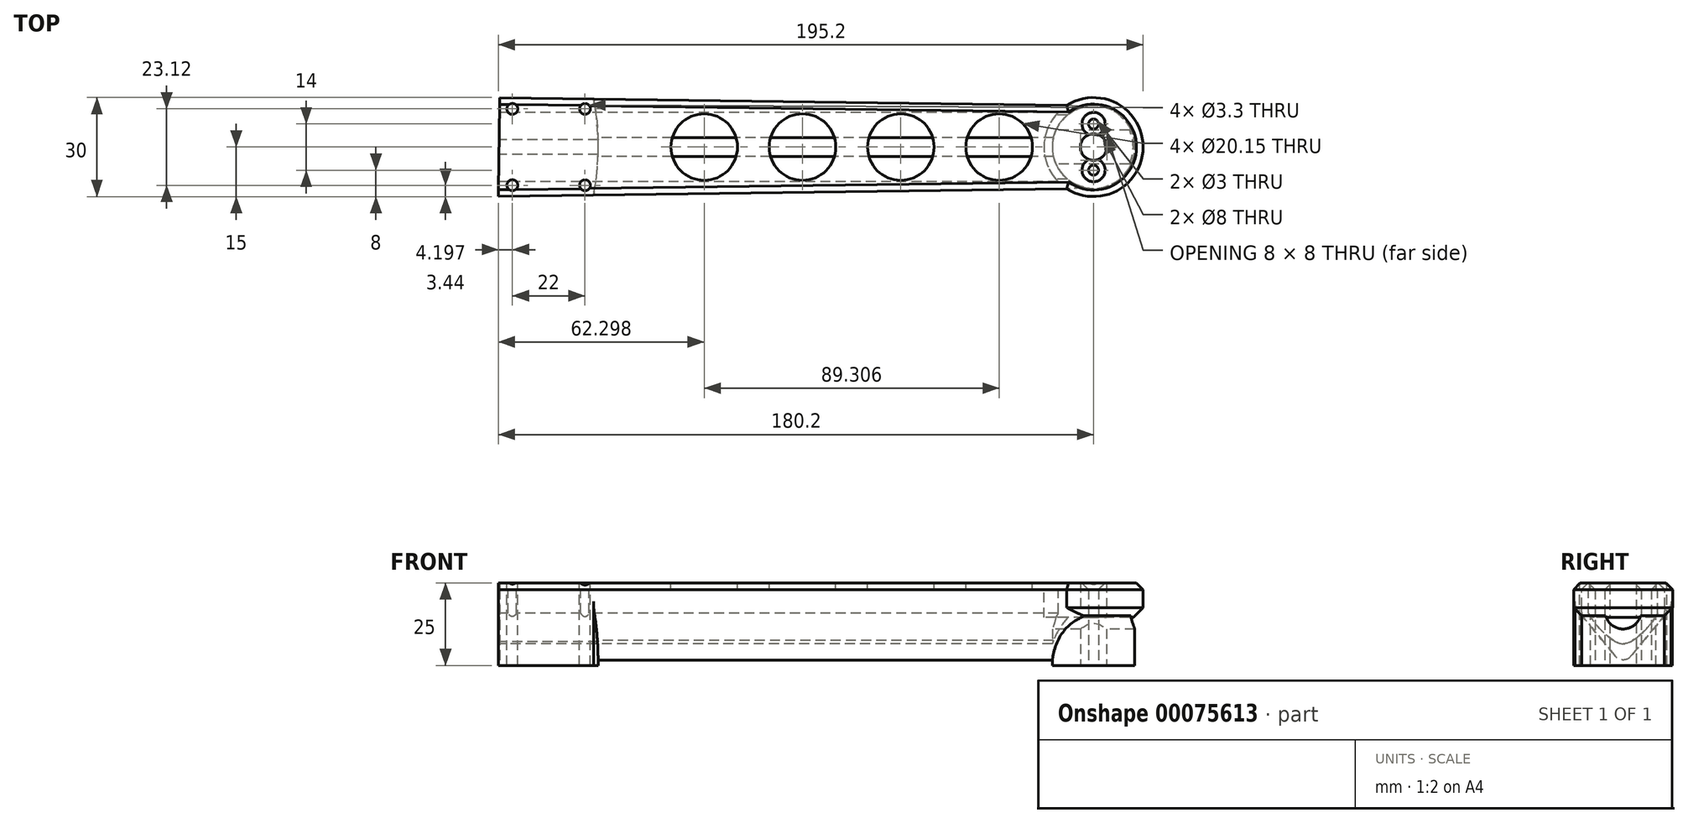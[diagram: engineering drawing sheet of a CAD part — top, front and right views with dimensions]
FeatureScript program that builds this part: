
annotation { "Feature Type Name" : "Feature", "Feature Type Description" : "" }
export const myFeature = defineFeature(function(context is Context, id is Id, definition is map)
    precondition{}
    {
        {
            var Q0;
            Q0=qCreatedBy(makeId("Top.planeOp"),FACE);
            var sketch = newSketch(context, id + "F0", { "sketchPlane" : qUnion([Q0])});
            skArc(sketch, "E0", {"start": v(73.58, -14.53) * mm, "mid": v(75, 0) * mm, "end": v(73.58, 14.53) * mm});
            skCircle(sketch, "E1", {"center": v(225, 0) * mm, "radius": 12.5 * mm});
            skLineSegment(sketch, "E2", {"start": v(224.65, 12.5) * mm, "end": v(45.2, 14.9) * mm});
            skLineSegment(sketch, "E3.MirrorCS", {"start": v(224.65, -12.5) * mm, "end": v(44.8, -14.91) * mm});
            skLineSegment(sketch, "E4", {"start": v(45.2, 14.9) * mm, "end": v(44.8, -14.91) * mm});
            skPoint(sketch, "E5.orphan", {"position": v(38.3, 15) * mm});
            skPoint(sketch, "E6.orphan", {"position": v(38.3, -15) * mm});
            skSolve(sketch);
        }
        {
            var Q0;
            {var subQ0=sQuery(id+"F0.wireOp",EDGE,"E0");Q0=makeQuery(id+"F0.imprint","IMPRINT",FACE,{"disambiguationData":[TD([[makeQuery(id+"F0.imprint","IMPRINT",EDGE,{"derivedFrom":subQ0}),-1.0]])]});}
            extrude(context, id + "F1", {"entities" : qUnion([Q0]), "depth" : 25 * mm});
        }
        {
            var Q0;
            Q0=qCreatedBy(makeId("Right.planeOp"),FACE);
            var sketch = newSketch(context, id + "F2", { "sketchPlane" : qUnion([Q0])});
            skLineSegment(sketch, "E7", {"start": v(-36.38, 18) * mm, "end": v(32.2, 18) * mm, "construction": true});
            skLineSegment(sketch, "E8", {"start": v(-14.91, 18) * mm, "end": v(-2.26, 2.72) * mm});
            skLineSegment(sketch, "E9.MirrorCS", {"start": v(14.91, 18) * mm, "end": v(2.26, 2.72) * mm});
            skPoint(sketch, "E10.visualSharp", {"position": v(0, 0) * mm});
            skArc(sketch, "E10.filletArc", {"start": v(-2.26, 2.72) * mm, "mid": v(0, 1.66) * mm, "end": v(2.26, 2.72) * mm});
            skLineSegment(sketch, "E11", {"start": v(14.91, 18) * mm, "end": v(14.91, -2.4) * mm});
            skLineSegment(sketch, "E12", {"start": v(14.91, -2.4) * mm, "end": v(-14.91, -2.4) * mm});
            skLineSegment(sketch, "E13", {"start": v(-14.91, -2.4) * mm, "end": v(-14.91, 18) * mm});
            skSolve(sketch);
        }
        {
            var Q0;
            Q0 = qSketchRegion(id + "F2", true);
            extrude(context, id + "F3", {"entities" : qUnion([Q0]), "operationType" : NewBodyOperationType.REMOVE, "endBound" : BoundingType.THROUGH_ALL, "depth" : 25 * mm});
        }
        {
            var Q0;
            Q0=qCreatedBy(makeId("Right.planeOp"),FACE);
            var sketch = newSketch(context, id + "F4", { "sketchPlane" : qUnion([Q0])});
            skLineSegment(sketch, "E14", {"start": v(10.5, 23) * mm, "end": v(-10.5, 23) * mm});
            skPoint(sketch, "E15.orphan", {"position": v(12.88, 17.57) * mm});
            skPoint(sketch, "E16.orphan", {"position": v(-12.88, 17.57) * mm});
            skArc(sketch, "E17", {"start": v(-2.82, 7.54) * mm, "mid": v(0, 6.6) * mm, "end": v(2.82, 7.54) * mm});
            skLineSegment(sketch, "E18", {"start": v(-10.5, 23) * mm, "end": v(-10.5, 15.85) * mm});
            skLineSegment(sketch, "E19.MirrorCS", {"start": v(10.5, 23) * mm, "end": v(10.5, 15.85) * mm});
            skPoint(sketch, "E20.orphan", {"position": v(-12.88, 23) * mm});
            skPoint(sketch, "E21.orphan", {"position": v(-10.5, 23.41) * mm});
            skPoint(sketch, "E22.orphan", {"position": v(-10.5, 15.28) * mm});
            skPoint(sketch, "E23.end.orphan", {"position": v(12.88, 23) * mm});
            skPoint(sketch, "E24.orphan", {"position": v(10.5, 15.28) * mm});
            skPoint(sketch, "E25.orphan", {"position": v(10.5, 23.41) * mm});
            skArc(sketch, "E26", {"start": v(2.2, 7.15) * mm, "mid": v(6.91, 10.96) * mm, "end": v(10.5, 15.85) * mm});
            skArc(sketch, "E27.MirrorCS", {"start": v(-2.2, 7.15) * mm, "mid": v(-6.91, 10.96) * mm, "end": v(-10.5, 15.85) * mm});
            skPoint(sketch, "E28.center.orphan", {"position": v(0, 25.65) * mm});
            skSolve(sketch);
        }
        {
            var Q0;
            Q0 = qSketchRegion(id + "F4", true);
            extrude(context, id + "F5", {"entities" : qUnion([Q0]), "operationType" : NewBodyOperationType.REMOVE, "endBound" : BoundingType.THROUGH_ALL, "depth" : 25 * mm, "hasSecondDirection" : true, "secondDirectionBound" : SecondDirectionBoundingType.THROUGH_ALL, "secondDirectionOppositeDirection" : true, "secondDirectionDepth" : 25 * mm});
        }
        {
            var Q0;
            Q0=makeQuery(id+"F1.opExtrude","CAP_FACE",FACE,{"disambiguationData":[OSD([sQuery(id+"F0.wireOp",EDGE,"E0"),sQuery(id+"F0.wireOp",EDGE,"E1"),sQuery(id+"F0.wireOp",EDGE,"E2"),sQuery(id+"F0.wireOp",EDGE,"E3.MirrorCS")])],"isStart":false});
            var sketch = newSketch(context, id + "F6", { "sketchPlane" : qUnion([Q0])});
            skCircle(sketch, "E29", {"center": v(107.1, 0) * mm, "radius": 10.07 * mm});
            skCircle(sketch, "E30.1.0.0", {"center": v(136.87, 0) * mm, "radius": 10.07 * mm});
            skCircle(sketch, "E30.2.0.0", {"center": v(166.64, 0) * mm, "radius": 10.07 * mm});
            skCircle(sketch, "E30.3.0.0", {"center": v(196.4, 0) * mm, "radius": 10.07 * mm});
            skLineSegment(sketch, "E30.direction1", {"start": v(107.1, 0) * mm, "end": v(136.87, 0) * mm, "construction": true});
            skSolve(sketch);
        }
        {
            var Q0;
            Q0=makeQuery(id+"F6.imprint","IMPRINT",FACE,{"disambiguationData":[TD([[makeQuery(id+"F6.imprint","IMPRINT",EDGE,{"derivedFrom":sQuery(id+"F6.wireOp",EDGE,"E30.3.0.0")}),1.0]])]});
            var Q1;
            Q1=makeQuery(id+"F6.imprint","IMPRINT",FACE,{"disambiguationData":[TD([[makeQuery(id+"F6.imprint","IMPRINT",EDGE,{"derivedFrom":sQuery(id+"F6.wireOp",EDGE,"E30.2.0.0")}),1.0]])]});
            var Q2;
            Q2=makeQuery(id+"F6.imprint","IMPRINT",FACE,{"disambiguationData":[TD([[makeQuery(id+"F6.imprint","IMPRINT",EDGE,{"derivedFrom":sQuery(id+"F6.wireOp",EDGE,"E30.1.0.0")}),1.0]])]});
            var Q3;
            Q3=makeQuery(id+"F6.imprint","IMPRINT",FACE,{"disambiguationData":[TD([[makeQuery(id+"F6.imprint","IMPRINT",EDGE,{"derivedFrom":sQuery(id+"F6.wireOp",EDGE,"E29")}),1.0]])]});
            var Q4;
            Q4=makeQuery(id+"F5.boolean.opBoolean","COPY",FACE,{"derivedFrom":makeQuery(id+"F5.opExtrude","SWEPT_FACE",FACE,{"disambiguationData":[OSD([sQuery(id+"F4.wireOp",EDGE,"E17")])]})});
            extrude(context, id + "F7", {"entities" : qUnion([Q0, Q1, Q2, Q3]), "operationType" : NewBodyOperationType.REMOVE, "oppositeDirection" : true, "endBoundEntityFace" : qUnion([Q4]), "depth" : 7.95 * mm});
        }
        {
            var Q0;
            {var subQ0=sQuery(id+"F0.wireOp",EDGE,"E1");var subQ1=makeQuery(id+"F0.imprint","INTERSECT",VERTEX,{"derivedFrom":[subQ0,sQuery(id+"F0.wireOp",EDGE,"E2")]});Q0=makeQuery(id+"F0.imprint","IMPRINT",FACE,{"disambiguationData":[TD([[makeQuery(id+"F0.imprint","IMPRINT",EDGE,{"disambiguationData":[TD([[subQ1,-1.0]])],"derivedFrom":subQ0}),1.0]])]});}
            extrude(context, id + "F8", {"entities" : qUnion([Q0]), "operationType" : NewBodyOperationType.REMOVE, "depth" : 15.03 * mm});
        }
        {
            var Q0;
            {var subQ0=sQuery(id+"F0.wireOp",EDGE,"E0");Q0=makeQuery(id+"F0.imprint","IMPRINT",FACE,{"disambiguationData":[TD([[makeQuery(id+"F0.imprint","IMPRINT",EDGE,{"derivedFrom":subQ0}),1.0]])]});}
            extrude(context, id + "F9", {"entities" : qUnion([Q0]), "operationType" : NewBodyOperationType.ADD, "depth" : 25 * mm});
        }
        {
            var Q0;
            {var subQ0=sQuery(id+"F0.wireOp",EDGE,"E3.MirrorCS");var subQ1=sQuery(id+"F0.wireOp",EDGE,"E2");var subQ2=sQuery(id+"F0.wireOp",EDGE,"E0");var subQ3=sQuery(id+"F0.wireOp",EDGE,"E1");Q0=makeQuery(id+"F9.boolean.opBoolean","MERGE",FACE,{"derivedFrom":[makeQuery(id+"FpcsPqxv3NGoszD_1.boolean.opBoolean","MERGE",FACE,{"derivedFrom":[makeQuery(id+"F1.opExtrude","CAP_FACE",FACE,{"disambiguationData":[OSD([subQ2,subQ3,subQ1,subQ0])],"isStart":false}),makeQuery(id+"FpcsPqxv3NGoszD_1.opExtrude","CAP_FACE",FACE,{"disambiguationData":[OSD([subQ3])],"isStart":false})]}),makeQuery(id+"F9.opExtrude","CAP_FACE",FACE,{"disambiguationData":[OSD([subQ2,subQ1,subQ0,sQuery(id+"F0.wireOp",EDGE,"E4")])],"isStart":false})]});}
            var sketch = newSketch(context, id + "F10", { "sketchPlane" : qUnion([Q0])});
            skCircle(sketch, "E31", {"center": v(49, 11.56) * mm, "radius": 1.65 * mm});
            skCircle(sketch, "E32", {"center": v(71, 11.56) * mm, "radius": 1.65 * mm});
            skCircle(sketch, "E33.MirrorC", {"center": v(49, -11.56) * mm, "radius": 1.65 * mm});
            skCircle(sketch, "E34.MirrorC", {"center": v(71, -11.56) * mm, "radius": 1.65 * mm});
            skSolve(sketch);
        }
        {
            var Q0;
            Q0 = qSketchRegion(id + "F10", true);
            extrude(context, id + "F11", {"entities" : qUnion([Q0]), "operationType" : NewBodyOperationType.REMOVE, "oppositeDirection" : true, "depth" : 25 * mm});
        }
        {
            var Q0;
            {var subQ0=sQuery(id+"F0.wireOp",EDGE,"E3.MirrorCS");var subQ1=sQuery(id+"F0.wireOp",EDGE,"E2");var subQ2=sQuery(id+"F0.wireOp",EDGE,"E0");var subQ3=sQuery(id+"F0.wireOp",EDGE,"E1");Q0=makeQuery(id+"F9.boolean.opBoolean","MERGE",FACE,{"derivedFrom":[makeQuery(id+"FpcsPqxv3NGoszD_1.boolean.opBoolean","MERGE",FACE,{"derivedFrom":[makeQuery(id+"F1.opExtrude","CAP_FACE",FACE,{"disambiguationData":[OSD([subQ2,subQ3,subQ1,subQ0])],"isStart":false}),makeQuery(id+"FpcsPqxv3NGoszD_1.opExtrude","CAP_FACE",FACE,{"disambiguationData":[OSD([subQ3])],"isStart":false})]}),makeQuery(id+"F9.opExtrude","CAP_FACE",FACE,{"disambiguationData":[OSD([subQ2,subQ1,subQ0,sQuery(id+"F0.wireOp",EDGE,"E4")])],"isStart":false})]});}
            var sketch = newSketch(context, id + "F12", { "sketchPlane" : qUnion([Q0])});
            skCircle(sketch, "E35", {"center": v(225, 0) * mm, "radius": 3 * mm});
            skCircle(sketch, "E36", {"center": v(225, 7) * mm, "radius": 1.5 * mm});
            skCircle(sketch, "E37", {"center": v(225, -7) * mm, "radius": 1.5 * mm});
            skSolve(sketch);
        }
        {
            var Q0;
            Q0 = qSketchRegion(id + "F12", true);
            extrude(context, id + "F13", {"entities" : qUnion([Q0]), "operationType" : NewBodyOperationType.REMOVE, "oppositeDirection" : true, "depth" : 25 * mm});
        }
        {
            var Q0;
            Q0=makeQuery(id+"F4.imprint","IMPRINT",FACE,{"disambiguationData":[TD([[makeQuery(id+"F4.imprint","IMPRINT",EDGE,{"derivedFrom":sQuery(id+"F4.wireOp",EDGE,"E14")}),1.0]])]});
            extrude(context, id + "F14", {"entities" : qUnion([Q0]), "operationType" : NewBodyOperationType.REMOVE, "depth" : 84.6 * mm});
        }
        {
            var Q0;
            {var subQ0=sQuery(id+"F0.wireOp",EDGE,"E1");var subQ1=makeQuery(id+"F0.imprint","INTERSECT",VERTEX,{"derivedFrom":[subQ0,sQuery(id+"F0.wireOp",EDGE,"E2")]});Q0=makeQuery(id+"F0.imprint","IMPRINT",FACE,{"disambiguationData":[TD([[makeQuery(id+"F0.imprint","IMPRINT",EDGE,{"disambiguationData":[TD([[subQ1,-1.0]])],"derivedFrom":subQ0}),1.0]])]});}
            extrude(context, id + "F15", {"entities" : qUnion([Q0]), "operationType" : NewBodyOperationType.ADD, "depth" : 25 * mm});
        }
        {
            var Q0;
            Q0=qCreatedBy(makeId("Right.planeOp"),FACE);
            var sketch = newSketch(context, id + "F16", { "sketchPlane" : qUnion([Q0])});
            skCircle(sketch, "E38", {"center": v(0, 16.54) * mm, "radius": 5.49 * mm});
            skSolve(sketch);
        }
        {
            var Q0;
            Q0 = qSketchRegion(id + "F16", true);
            extrude(context, id + "F17", {"entities" : qUnion([Q0]), "operationType" : NewBodyOperationType.REMOVE, "endBound" : BoundingType.THROUGH_ALL, "depth" : 25 * mm});
        }
        {
            var Q0;
            {var subQ0=sQuery(id+"F0.wireOp",EDGE,"E1");var subQ1=makeQuery(id+"F0.imprint","INTERSECT",VERTEX,{"derivedFrom":[subQ0,sQuery(id+"F0.wireOp",EDGE,"E2")]});Q0=makeQuery(id+"F0.imprint","IMPRINT",FACE,{"disambiguationData":[TD([[makeQuery(id+"F0.imprint","IMPRINT",EDGE,{"disambiguationData":[TD([[subQ1,-1.0]])],"derivedFrom":subQ0}),1.0]])]});}
            var sketch = newSketch(context, id + "F18", { "sketchPlane" : qUnion([Q0])});
            skCircle(sketch, "E39", {"center": v(225, 0) * mm, "radius": 4 * mm});
            skCircle(sketch, "E40", {"center": v(225, -7) * mm, "radius": 1.5 * mm});
            skCircle(sketch, "E41", {"center": v(225, 7) * mm, "radius": 1.5 * mm});
            skSolve(sketch);
        }
        {
            var Q0;
            Q0 = qSketchRegion(id + "F18", true);
            extrude(context, id + "F19", {"entities" : qUnion([Q0]), "operationType" : NewBodyOperationType.REMOVE, "endBound" : BoundingType.THROUGH_ALL, "depth" : 25 * mm});
        }
        {
            var Q0;
            {var subQ0=sQuery(id+"F0.wireOp",EDGE,"E1");var subQ1=sQuery(id+"F0.wireOp",EDGE,"E3.MirrorCS");var subQ2=sQuery(id+"F0.wireOp",EDGE,"E2");var subQ3=sQuery(id+"F0.wireOp",EDGE,"E0");Q0=makeQuery(id+"F19.boolean.opBoolean","INTERSECT",EDGE,{"derivedFrom":[makeQuery(id+"F15.boolean.opBoolean","MERGE",FACE,{"derivedFrom":[makeQuery(id+"F9.boolean.opBoolean","MERGE",FACE,{"derivedFrom":[makeQuery(id+"F1.opExtrude","CAP_FACE",FACE,{"disambiguationData":[OSD([subQ3,subQ0,subQ2,subQ1])],"isStart":false}),makeQuery(id+"F9.opExtrude","CAP_FACE",FACE,{"disambiguationData":[OSD([subQ3,subQ2,subQ1,sQuery(id+"F0.wireOp",EDGE,"E4")])],"isStart":false})]}),makeQuery(id+"F15.opExtrude","CAP_FACE",FACE,{"disambiguationData":[OSD([subQ0])],"isStart":false})]}),makeQuery(id+"F19.opExtrude","SWEPT_FACE",FACE,{"disambiguationData":[OSD([sQuery(id+"F18.wireOp",EDGE,"E40")])]})]});}
            var Q1;
            {var subQ0=sQuery(id+"F0.wireOp",EDGE,"E1");var subQ1=sQuery(id+"F0.wireOp",EDGE,"E3.MirrorCS");var subQ2=sQuery(id+"F0.wireOp",EDGE,"E2");var subQ3=sQuery(id+"F0.wireOp",EDGE,"E0");Q1=makeQuery(id+"F19.boolean.opBoolean","INTERSECT",EDGE,{"derivedFrom":[makeQuery(id+"F15.boolean.opBoolean","MERGE",FACE,{"derivedFrom":[makeQuery(id+"F9.boolean.opBoolean","MERGE",FACE,{"derivedFrom":[makeQuery(id+"F1.opExtrude","CAP_FACE",FACE,{"disambiguationData":[OSD([subQ3,subQ0,subQ2,subQ1])],"isStart":false}),makeQuery(id+"F9.opExtrude","CAP_FACE",FACE,{"disambiguationData":[OSD([subQ3,subQ2,subQ1,sQuery(id+"F0.wireOp",EDGE,"E4")])],"isStart":false})]}),makeQuery(id+"F15.opExtrude","CAP_FACE",FACE,{"disambiguationData":[OSD([subQ0])],"isStart":false})]}),makeQuery(id+"F19.opExtrude","SWEPT_FACE",FACE,{"disambiguationData":[OSD([sQuery(id+"F18.wireOp",EDGE,"E41")])]})]});}
            chamfer(context, id + "F20", {"entities" : qUnion([Q0, Q1]), "width" : 2 * mm, "tangentPropagation" : true});
        }
        {
            var Q0;
            Q0=makeQuery(id+"F3.boolean.opBoolean","INTERSECT",EDGE,{"derivedFrom":[makeQuery(id+"F1.opExtrude","SWEPT_FACE",FACE,{"disambiguationData":[OSD([sQuery(id+"F0.wireOp",EDGE,"E3.MirrorCS")])]}),makeQuery(id+"F3.opExtrude","SWEPT_FACE",FACE,{"disambiguationData":[OSD([sQuery(id+"F2.wireOp",EDGE,"E8")])]})]});
            var Q1;
            Q1=makeQuery(id+"F3.boolean.opBoolean","INTERSECT",EDGE,{"derivedFrom":[makeQuery(id+"F1.opExtrude","SWEPT_FACE",FACE,{"disambiguationData":[OSD([sQuery(id+"F0.wireOp",EDGE,"E2")])]}),makeQuery(id+"F3.opExtrude","SWEPT_FACE",FACE,{"disambiguationData":[OSD([sQuery(id+"F2.wireOp",EDGE,"E9.MirrorCS")])]})]});
            fillet(context, id + "F21", {"entities" : qUnion([Q0, Q1]), "radius" : 5 * mm, "tangentPropagation" : true, "allowEdgeOverflow" : false});
        }
        {
            var Q0;
            {var subQ0=sQuery(id+"F0.wireOp",EDGE,"E3.MirrorCS");Q0=makeQuery(id+"F9.boolean.opBoolean","MERGE",EDGE,{"derivedFrom":[makeQuery(id+"F1.opExtrude","CAP_EDGE",EDGE,{"disambiguationData":[OSD([subQ0])],"isStart":false}),makeQuery(id+"F9.opExtrude","CAP_EDGE",EDGE,{"disambiguationData":[OSD([subQ0])],"isStart":false})]});}
            var Q1;
            {var subQ0=sQuery(id+"F0.wireOp",EDGE,"E2");Q1=makeQuery(id+"F9.boolean.opBoolean","MERGE",EDGE,{"derivedFrom":[makeQuery(id+"F1.opExtrude","CAP_EDGE",EDGE,{"disambiguationData":[OSD([subQ0])],"isStart":false}),makeQuery(id+"F9.opExtrude","CAP_EDGE",EDGE,{"disambiguationData":[OSD([subQ0])],"isStart":false})]});}
            var Q2;
            Q2=makeQuery(id+"F15.opExtrude","CAP_EDGE",EDGE,{"disambiguationData":[OSD([sQuery(id+"F0.wireOp",EDGE,"E1")])],"isStart":false});
            chamfer(context, id + "F22", {"entities" : qUnion([Q0, Q1, Q2]), "width" : 2 * mm, "tangentPropagation" : true});
        }
        {
            var Q0;
            {var subQ0=sQuery(id+"F0.wireOp",EDGE,"E1");var subQ1=sQuery(id+"F0.wireOp",EDGE,"E3.MirrorCS");var subQ2=sQuery(id+"F0.wireOp",EDGE,"E2");var subQ3=sQuery(id+"F0.wireOp",EDGE,"E0");Q0=makeQuery(id+"F22.opChamfer","SPLIT",FACE,{"disambiguationData":[OD(0.0)],"derivedFrom":makeQuery(id+"F15.boolean.opBoolean","MERGE",FACE,{"derivedFrom":[makeQuery(id+"F9.boolean.opBoolean","MERGE",FACE,{"derivedFrom":[makeQuery(id+"F1.opExtrude","CAP_FACE",FACE,{"disambiguationData":[OSD([subQ3,subQ0,subQ2,subQ1])],"isStart":false}),makeQuery(id+"F9.opExtrude","CAP_FACE",FACE,{"disambiguationData":[OSD([subQ3,subQ2,subQ1,sQuery(id+"F0.wireOp",EDGE,"E4")])],"isStart":false})]}),makeQuery(id+"F15.opExtrude","CAP_FACE",FACE,{"disambiguationData":[OSD([subQ0])],"isStart":false})]})});}
            var sketch = newSketch(context, id + "F23", { "sketchPlane" : qUnion([Q0])});
            skCircle(sketch, "E42", {"center": v(225, 0) * mm, "radius": 15 * mm});
            skSolve(sketch);
        }
        {
            var Q0;
            Q0 = qSketchRegion(id + "F23", true);
            extrude(context, id + "F24", {"entities" : qUnion([Q0]), "operationType" : NewBodyOperationType.ADD, "oppositeDirection" : true, "depth" : 10.48 * mm});
        }
        {
            var Q0;
            Q0=makeQuery(id+"F18.imprint","IMPRINT",FACE,{"disambiguationData":[TD([[makeQuery(id+"F18.imprint","IMPRINT",EDGE,{"derivedFrom":sQuery(id+"F18.wireOp",EDGE,"E40")}),1.0]])]});
            var Q1;
            Q1=makeQuery(id+"F18.imprint","IMPRINT",FACE,{"disambiguationData":[TD([[makeQuery(id+"F18.imprint","IMPRINT",EDGE,{"derivedFrom":sQuery(id+"F18.wireOp",EDGE,"E41")}),1.0]])]});
            var Q2;
            Q2=makeQuery(id+"F18.imprint","IMPRINT",FACE,{"disambiguationData":[TD([[makeQuery(id+"F18.imprint","IMPRINT",EDGE,{"derivedFrom":sQuery(id+"F18.wireOp",EDGE,"E39")}),1.0]])]});
            extrude(context, id + "F25", {"entities" : qUnion([Q0, Q1, Q2]), "operationType" : NewBodyOperationType.REMOVE, "endBound" : BoundingType.THROUGH_ALL, "depth" : 25 * mm});
        }
        {
            var Q0;
            {var subQ0=sQuery(id+"F0.wireOp",EDGE,"E1");var subQ1=sQuery(id+"F0.wireOp",EDGE,"E3.MirrorCS");var subQ2=sQuery(id+"F0.wireOp",EDGE,"E2");var subQ3=sQuery(id+"F0.wireOp",EDGE,"E0");var subQ4=makeQuery(id+"F15.boolean.opBoolean","MERGE",FACE,{"derivedFrom":[makeQuery(id+"F9.boolean.opBoolean","MERGE",FACE,{"derivedFrom":[makeQuery(id+"F1.opExtrude","CAP_FACE",FACE,{"disambiguationData":[OSD([subQ3,subQ0,subQ2,subQ1])],"isStart":false}),makeQuery(id+"F9.opExtrude","CAP_FACE",FACE,{"disambiguationData":[OSD([subQ3,subQ2,subQ1,sQuery(id+"F0.wireOp",EDGE,"E4")])],"isStart":false})]}),makeQuery(id+"F15.opExtrude","CAP_FACE",FACE,{"disambiguationData":[OSD([subQ0])],"isStart":false})]});Q0=makeQuery(id+"F25.boolean.opBoolean","INTERSECT",EDGE,{"derivedFrom":[makeQuery(id+"F24.boolean.opBoolean","MERGE",FACE,{"derivedFrom":[makeQuery(id+"F22.opChamfer","SPLIT",FACE,{"disambiguationData":[OD(0.0)],"derivedFrom":subQ4}),makeQuery(id+"F22.opChamfer","SPLIT",FACE,{"disambiguationData":[OD(1.0)],"derivedFrom":subQ4}),makeQuery(id+"F24.opExtrude","CAP_FACE",FACE,{"disambiguationData":[OSD([sQuery(id+"F23.wireOp",EDGE,"E42")])],"isStart":true})]}),makeQuery(id+"F25.opExtrude","SWEPT_FACE",FACE,{"disambiguationData":[OSD([sQuery(id+"F18.wireOp",EDGE,"E40")])]})]});}
            var Q1;
            {var subQ0=sQuery(id+"F0.wireOp",EDGE,"E1");var subQ1=sQuery(id+"F0.wireOp",EDGE,"E3.MirrorCS");var subQ2=sQuery(id+"F0.wireOp",EDGE,"E2");var subQ3=sQuery(id+"F0.wireOp",EDGE,"E0");var subQ4=makeQuery(id+"F15.boolean.opBoolean","MERGE",FACE,{"derivedFrom":[makeQuery(id+"F9.boolean.opBoolean","MERGE",FACE,{"derivedFrom":[makeQuery(id+"F1.opExtrude","CAP_FACE",FACE,{"disambiguationData":[OSD([subQ3,subQ0,subQ2,subQ1])],"isStart":false}),makeQuery(id+"F9.opExtrude","CAP_FACE",FACE,{"disambiguationData":[OSD([subQ3,subQ2,subQ1,sQuery(id+"F0.wireOp",EDGE,"E4")])],"isStart":false})]}),makeQuery(id+"F15.opExtrude","CAP_FACE",FACE,{"disambiguationData":[OSD([subQ0])],"isStart":false})]});Q1=makeQuery(id+"F25.boolean.opBoolean","INTERSECT",EDGE,{"derivedFrom":[makeQuery(id+"F24.boolean.opBoolean","MERGE",FACE,{"derivedFrom":[makeQuery(id+"F22.opChamfer","SPLIT",FACE,{"disambiguationData":[OD(0.0)],"derivedFrom":subQ4}),makeQuery(id+"F22.opChamfer","SPLIT",FACE,{"disambiguationData":[OD(1.0)],"derivedFrom":subQ4}),makeQuery(id+"F24.opExtrude","CAP_FACE",FACE,{"disambiguationData":[OSD([sQuery(id+"F23.wireOp",EDGE,"E42")])],"isStart":true})]}),makeQuery(id+"F25.opExtrude","SWEPT_FACE",FACE,{"disambiguationData":[OSD([sQuery(id+"F18.wireOp",EDGE,"E41")])]})]});}
            var Q2;
            Q2=makeQuery(id+"F24.opExtrude","CAP_EDGE",EDGE,{"disambiguationData":[OSD([sQuery(id+"F23.wireOp",EDGE,"E42")])],"isStart":true});
            chamfer(context, id + "F26", {"entities" : qUnion([Q0, Q1, Q2]), "width" : 2 * mm, "tangentPropagation" : true});
        }
        {
            var Q0;
            {var subQ0=sQuery(id+"F23.wireOp",EDGE,"E42");Q0=makeQuery(id+"F24.boolean.opBoolean","SPLIT",EDGE,{"disambiguationData":[TD([makeQuery(id+"F21.opFillet","BLEND_FACE",FACE,{"disambiguationData":[OSD([sQuery(id+"F0.wireOp",EDGE,"E3.MirrorCS"),sQuery(id+"F2.wireOp",EDGE,"E8")])]})])],"derivedFrom":makeQuery(id+"F24.opExtrude","CAP_EDGE",EDGE,{"disambiguationData":[OSD([subQ0])],"isStart":false})});}
            chamfer(context, id + "F27", {"entities" : qUnion([Q0]), "width" : 3 * mm, "tangentPropagation" : true});
        }
    });
